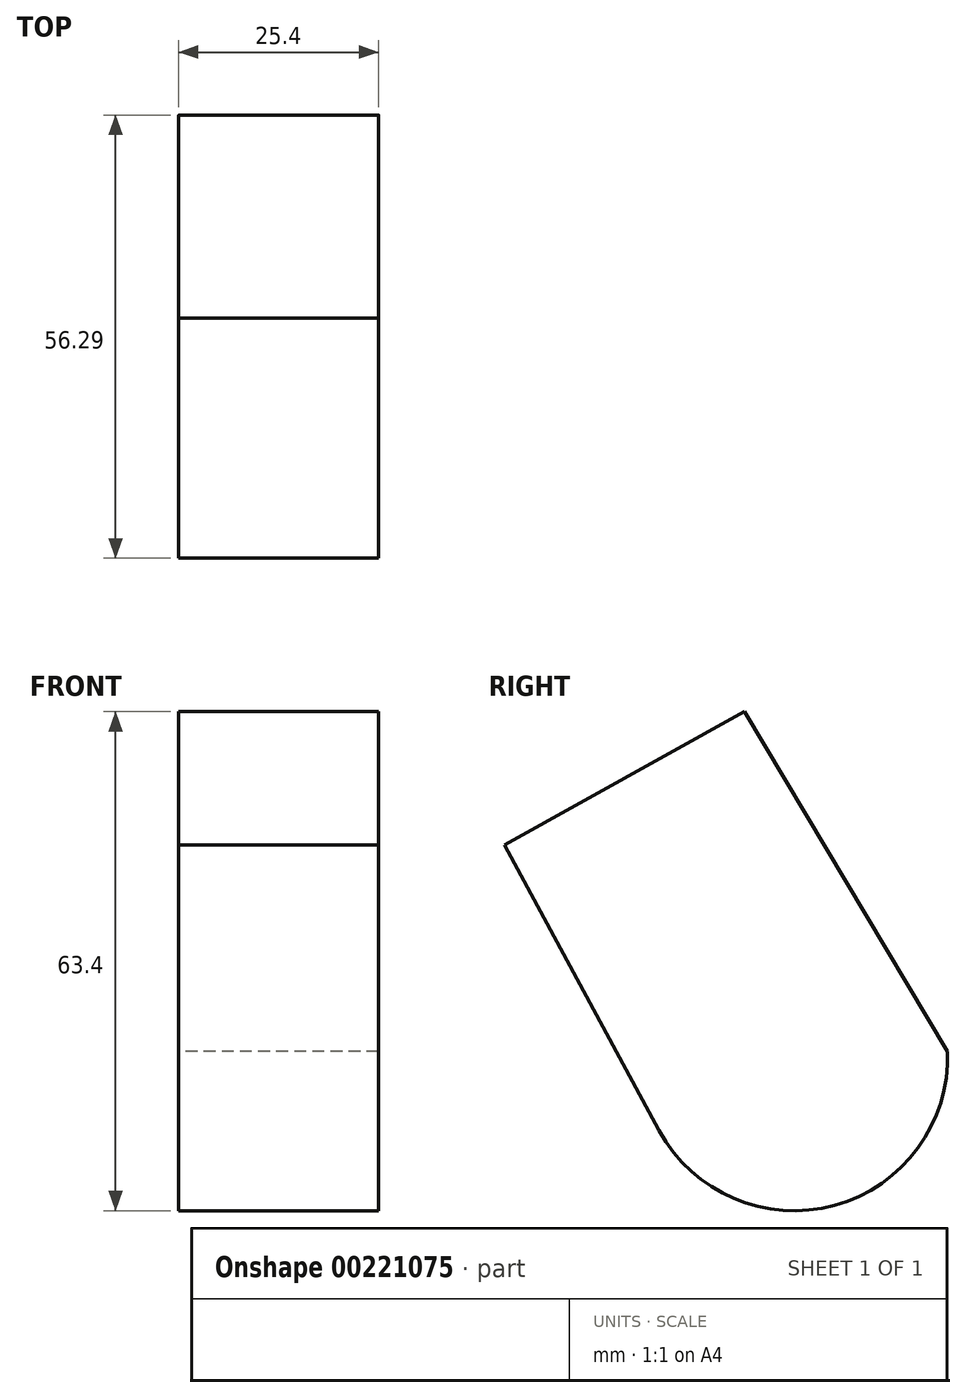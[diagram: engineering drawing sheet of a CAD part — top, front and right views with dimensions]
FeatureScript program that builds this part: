
annotation { "Feature Type Name" : "Feature", "Feature Type Description" : "" }
export const myFeature = defineFeature(function(context is Context, id is Id, definition is map)
    precondition{}
    {
        {
            var Q0;
            Q0=qCreatedBy(makeId("Right.planeOp"),FACE);
            var sketch = newSketch(context, id + "F0", { "sketchPlane" : qUnion([Q0])});
            skArc(sketch, "E0", {"start": v(0, -26.25) * mm, "mid": v(22.3, -35.77) * mm, "end": v(36.63, -16.23) * mm});
            skLineSegment(sketch, "E1", {"start": v(36.63, -16.23) * mm, "end": v(10.85, 26.94) * mm});
            skLineSegment(sketch, "E2", {"start": v(0, -26.25) * mm, "end": v(-19.65, 10.03) * mm});
            skLineSegment(sketch, "E3", {"start": v(-19.65, 10.03) * mm, "end": v(10.85, 26.94) * mm});
            skSolve(sketch);
        }
        {
            var Q0;
            Q0 = qSketchRegion(id + "F0", true);
            extrude(context, id + "F1", {"entities" : qUnion([Q0]), "depth" : 25.4 * mm});
        }
    });
